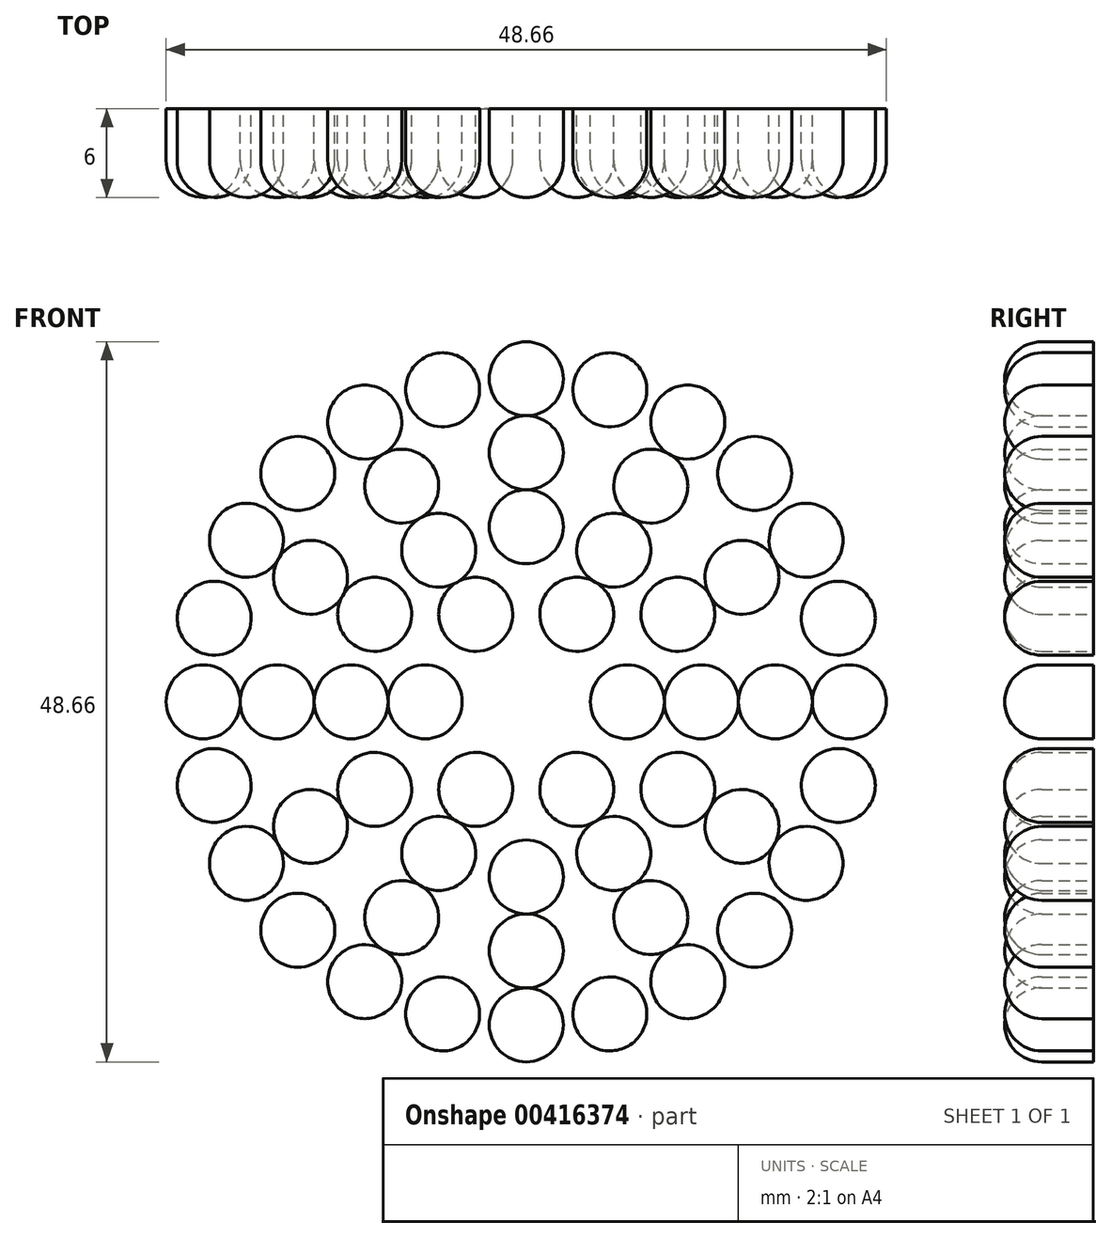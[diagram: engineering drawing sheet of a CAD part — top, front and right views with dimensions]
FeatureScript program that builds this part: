
annotation { "Feature Type Name" : "Feature", "Feature Type Description" : "" }
export const myFeature = defineFeature(function(context is Context, id is Id, definition is map)
    precondition{}
    {
        {
            var Q0;
            Q0=qCreatedBy(makeId("Front.planeOp"),FACE);
            var sketch = newSketch(context, id + "F0", { "sketchPlane" : qUnion([Q0])});
            skCircle(sketch, "E0.cCircle", {"center": v(0, 0) * mm, "radius": 9.33 * mm, "construction": true});
            skLineSegment(sketch, "E0.0", {"start": v(9.33, 2.5) * mm, "end": v(9.33, -2.5) * mm});
            skLineSegment(sketch, "E0.1", {"start": v(9.33, -2.5) * mm, "end": v(6.83, -6.83) * mm});
            skLineSegment(sketch, "E0.2", {"start": v(6.83, -6.83) * mm, "end": v(2.5, -9.33) * mm});
            skLineSegment(sketch, "E0.3", {"start": v(2.5, -9.33) * mm, "end": v(-2.5, -9.33) * mm});
            skLineSegment(sketch, "E0.4", {"start": v(-2.5, -9.33) * mm, "end": v(-6.83, -6.83) * mm});
            skLineSegment(sketch, "E0.5", {"start": v(-6.83, -6.83) * mm, "end": v(-9.33, -2.5) * mm});
            skLineSegment(sketch, "E0.6", {"start": v(-9.33, -2.5) * mm, "end": v(-9.33, 2.5) * mm});
            skLineSegment(sketch, "E0.7", {"start": v(-9.33, 2.5) * mm, "end": v(-6.83, 6.83) * mm});
            skLineSegment(sketch, "E0.8", {"start": v(-6.83, 6.83) * mm, "end": v(-2.5, 9.33) * mm});
            skLineSegment(sketch, "E0.9", {"start": v(-2.5, 9.33) * mm, "end": v(2.5, 9.33) * mm});
            skLineSegment(sketch, "E0.10", {"start": v(2.5, 9.33) * mm, "end": v(6.83, 6.83) * mm});
            skLineSegment(sketch, "E0.11", {"start": v(6.83, 6.83) * mm, "end": v(9.33, 2.5) * mm});
            skPoint(sketch, "E0.0.midPoint", {"position": v(9.33, 0) * mm});
            skLineSegment(sketch, "E1", {"start": v(-9.33, 2.5) * mm, "end": v(-4.33, 2.5) * mm});
            skLineSegment(sketch, "E2", {"start": v(-4.33, 2.5) * mm, "end": v(-6.83, 6.83) * mm});
            skLineSegment(sketch, "E3", {"start": v(-2.5, 9.33) * mm, "end": v(0, 5) * mm});
            skLineSegment(sketch, "E4", {"start": v(0, 5) * mm, "end": v(2.5, 9.33) * mm});
            skLineSegment(sketch, "E5", {"start": v(9.33, 2.5) * mm, "end": v(4.33, 2.5) * mm});
            skLineSegment(sketch, "E6", {"start": v(4.33, 2.5) * mm, "end": v(6.83, 6.83) * mm});
            skLineSegment(sketch, "E7", {"start": v(9.33, -2.5) * mm, "end": v(4.33, -2.5) * mm});
            skLineSegment(sketch, "E8", {"start": v(4.33, -2.5) * mm, "end": v(6.83, -6.83) * mm});
            skLineSegment(sketch, "E9", {"start": v(-9.33, -2.5) * mm, "end": v(-4.33, -2.5) * mm});
            skLineSegment(sketch, "E10", {"start": v(-4.33, -2.5) * mm, "end": v(-6.83, -6.83) * mm});
            skLineSegment(sketch, "E11", {"start": v(-2.5, -9.33) * mm, "end": v(0, -5) * mm});
            skLineSegment(sketch, "E12", {"start": v(0, -5) * mm, "end": v(2.5, -9.33) * mm});
            skLineSegment(sketch, "E13", {"start": v(0, 5) * mm, "end": v(4.33, 2.5) * mm});
            skLineSegment(sketch, "E14", {"start": v(4.33, 2.5) * mm, "end": v(4.33, -2.5) * mm});
            skLineSegment(sketch, "E15", {"start": v(4.33, -2.5) * mm, "end": v(0, -5) * mm});
            skLineSegment(sketch, "E16", {"start": v(0, -5) * mm, "end": v(-4.33, -2.5) * mm});
            skLineSegment(sketch, "E17", {"start": v(-4.33, -2.5) * mm, "end": v(-4.33, 2.5) * mm});
            skLineSegment(sketch, "E18", {"start": v(-4.33, 2.5) * mm, "end": v(0, 5) * mm});
            skLineSegment(sketch, "E19", {"start": v(-2.5, 9.33) * mm, "end": v(-2.5, 14.33) * mm});
            skLineSegment(sketch, "E20", {"start": v(-2.5, 14.33) * mm, "end": v(2.5, 14.33) * mm});
            skLineSegment(sketch, "E21", {"start": v(2.5, 14.33) * mm, "end": v(2.5, 9.33) * mm});
            skLineSegment(sketch, "E22", {"start": v(2.5, 9.33) * mm, "end": v(5, 13.66) * mm});
            skLineSegment(sketch, "E23", {"start": v(5, 13.66) * mm, "end": v(9.33, 11.16) * mm});
            skLineSegment(sketch, "E24", {"start": v(9.33, 11.16) * mm, "end": v(6.83, 6.83) * mm});
            skLineSegment(sketch, "E25", {"start": v(6.83, 6.83) * mm, "end": v(11.16, 9.33) * mm});
            skLineSegment(sketch, "E26", {"start": v(11.16, 9.33) * mm, "end": v(13.66, 5) * mm});
            skLineSegment(sketch, "E27", {"start": v(13.66, 5) * mm, "end": v(9.33, 2.5) * mm});
            skLineSegment(sketch, "E28", {"start": v(9.33, 2.5) * mm, "end": v(14.33, 2.5) * mm});
            skLineSegment(sketch, "E29", {"start": v(14.33, 2.5) * mm, "end": v(14.33, -2.5) * mm});
            skLineSegment(sketch, "E30", {"start": v(14.33, -2.5) * mm, "end": v(9.33, -2.5) * mm});
            skLineSegment(sketch, "E31", {"start": v(9.33, -2.5) * mm, "end": v(13.66, -5) * mm});
            skLineSegment(sketch, "E32", {"start": v(13.66, -5) * mm, "end": v(11.16, -9.33) * mm});
            skLineSegment(sketch, "E33", {"start": v(11.16, -9.33) * mm, "end": v(6.83, -6.83) * mm});
            skLineSegment(sketch, "E34", {"start": v(6.83, -6.83) * mm, "end": v(9.33, -11.16) * mm});
            skLineSegment(sketch, "E35", {"start": v(9.33, -11.16) * mm, "end": v(5, -13.66) * mm});
            skLineSegment(sketch, "E36", {"start": v(5, -13.66) * mm, "end": v(2.5, -9.33) * mm});
            skLineSegment(sketch, "E37", {"start": v(2.5, -9.33) * mm, "end": v(2.5, -14.33) * mm});
            skLineSegment(sketch, "E38", {"start": v(2.5, -14.33) * mm, "end": v(-2.5, -14.33) * mm});
            skLineSegment(sketch, "E39", {"start": v(-2.5, -14.33) * mm, "end": v(-2.5, -9.33) * mm});
            skLineSegment(sketch, "E40", {"start": v(-2.5, -9.33) * mm, "end": v(-5, -13.66) * mm});
            skLineSegment(sketch, "E41", {"start": v(-5, -13.66) * mm, "end": v(-9.33, -11.16) * mm});
            skLineSegment(sketch, "E42", {"start": v(-9.33, -11.16) * mm, "end": v(-6.83, -6.83) * mm});
            skLineSegment(sketch, "E43", {"start": v(-6.83, -6.83) * mm, "end": v(-11.16, -9.33) * mm});
            skLineSegment(sketch, "E44", {"start": v(-11.16, -9.33) * mm, "end": v(-13.66, -5) * mm});
            skLineSegment(sketch, "E45", {"start": v(-13.66, -5) * mm, "end": v(-9.33, -2.5) * mm});
            skLineSegment(sketch, "E46", {"start": v(-9.33, -2.5) * mm, "end": v(-14.33, -2.5) * mm});
            skLineSegment(sketch, "E47", {"start": v(-14.33, -2.5) * mm, "end": v(-14.33, 2.5) * mm});
            skLineSegment(sketch, "E48", {"start": v(-14.33, 2.5) * mm, "end": v(-9.33, 2.5) * mm});
            skLineSegment(sketch, "E49", {"start": v(-9.33, 2.5) * mm, "end": v(-13.66, 5) * mm});
            skLineSegment(sketch, "E50", {"start": v(-13.66, 5) * mm, "end": v(-11.16, 9.33) * mm});
            skLineSegment(sketch, "E51", {"start": v(-11.16, 9.33) * mm, "end": v(-6.83, 6.83) * mm});
            skLineSegment(sketch, "E52", {"start": v(-6.83, 6.83) * mm, "end": v(-9.33, 11.16) * mm});
            skLineSegment(sketch, "E53", {"start": v(-9.33, 11.16) * mm, "end": v(-5, 13.66) * mm});
            skLineSegment(sketch, "E54", {"start": v(-5, 13.66) * mm, "end": v(-2.5, 9.33) * mm});
            skLineSegment(sketch, "E55", {"start": v(14.33, 2.5) * mm, "end": v(19.33, 2.5) * mm});
            skLineSegment(sketch, "E56", {"start": v(19.33, 2.5) * mm, "end": v(24.33, 2.5) * mm});
            skLineSegment(sketch, "E57", {"start": v(24.33, 2.5) * mm, "end": v(24.33, -2.5) * mm});
            skLineSegment(sketch, "E58", {"start": v(19.33, 2.5) * mm, "end": v(19.33, -2.5) * mm});
            skCircle(sketch, "E59", {"center": v(0, 0) * mm, "radius": 4.33 * mm});
            skLineSegment(sketch, "E60", {"start": v(6.83, -2.5) * mm, "end": v(6.83, 0) * mm});
            skLineSegment(sketch, "E61", {"start": v(11.83, -2.5) * mm, "end": v(11.83, 0) * mm});
            skLineSegment(sketch, "E62", {"start": v(14.33, -2.5) * mm, "end": v(19.33, -2.5) * mm});
            skLineSegment(sketch, "E63", {"start": v(24.33, -2.5) * mm, "end": v(19.33, -2.5) * mm});
            skLineSegment(sketch, "E64", {"start": v(16.83, -2.5) * mm, "end": v(16.83, 0) * mm});
            skLineSegment(sketch, "E65", {"start": v(21.83, -2.5) * mm, "end": v(21.83, 0) * mm});
            skCircle(sketch, "E66", {"center": v(6.83, 0) * mm, "radius": 2.5 * mm});
            skCircle(sketch, "E67", {"center": v(11.83, 0) * mm, "radius": 2.5 * mm});
            skCircle(sketch, "E68", {"center": v(16.83, 0) * mm, "radius": 2.5 * mm});
            skCircle(sketch, "E69", {"center": v(21.83, 0) * mm, "radius": 2.5 * mm});
            skSolve(sketch);
        }
        {
            var Q0;
            Q0=qCreatedBy(makeId("Right.planeOp"),FACE);
            var sketch = newSketch(context, id + "F1", { "sketchPlane" : qUnion([Q0])});
            skLineSegment(sketch, "E70", {"start": v(30.42, 0) * mm, "end": v(-36.01, 0) * mm});
            skSolve(sketch);
        }
        {
            var Q0;
            {var subQ0=sQuery(id+"F0.wireOp",EDGE,"E66");var subQ1=makeQuery(id+"F0.imprint","INTERSECT",VERTEX,{"derivedFrom":[sQuery(id+"F0.wireOp",EDGE,"E5"),subQ0]});Q0=makeQuery(id+"F0.imprint","IMPRINT",FACE,{"disambiguationData":[TD([[makeQuery(id+"F0.imprint","IMPRINT",EDGE,{"disambiguationData":[TD([[subQ1,-1.0]])],"derivedFrom":subQ0}),1.0]])]});}
            var Q1;
            {var subQ0=sQuery(id+"F0.wireOp",EDGE,"E67");var subQ1=makeQuery(id+"F0.imprint","INTERSECT",VERTEX,{"derivedFrom":[sQuery(id+"F0.wireOp",EDGE,"E28"),subQ0]});Q1=makeQuery(id+"F0.imprint","IMPRINT",FACE,{"disambiguationData":[TD([[makeQuery(id+"F0.imprint","IMPRINT",EDGE,{"disambiguationData":[TD([[subQ1,1.0]])],"derivedFrom":subQ0}),1.0]])]});}
            var Q2;
            {var subQ0=sQuery(id+"F0.wireOp",EDGE,"E68");var subQ1=makeQuery(id+"F0.imprint","INTERSECT",VERTEX,{"derivedFrom":[sQuery(id+"F0.wireOp",EDGE,"E55"),subQ0]});Q2=makeQuery(id+"F0.imprint","IMPRINT",FACE,{"disambiguationData":[TD([[makeQuery(id+"F0.imprint","IMPRINT",EDGE,{"disambiguationData":[TD([[subQ1,1.0]])],"derivedFrom":subQ0}),1.0]])]});}
            var Q3;
            {var subQ0=sQuery(id+"F0.wireOp",EDGE,"E69");var subQ1=makeQuery(id+"F0.imprint","INTERSECT",VERTEX,{"derivedFrom":[sQuery(id+"F0.wireOp",EDGE,"E56"),subQ0]});Q3=makeQuery(id+"F0.imprint","IMPRINT",FACE,{"disambiguationData":[TD([[makeQuery(id+"F0.imprint","IMPRINT",EDGE,{"disambiguationData":[TD([[subQ1,1.0]])],"derivedFrom":subQ0}),1.0]])]});}
            extrude(context, id + "F2", {"entities" : qUnion([Q0, Q1, Q2, Q3]), "depth" : 6 * mm});
        }
        {
            var Q0;
            Q0=makeQuery(id+"F2.opExtrude","CAP_EDGE",EDGE,{"disambiguationData":[OSD([sQuery(id+"F0.wireOp",EDGE,"E66")])],"isStart":false});
            var Q1;
            Q1=makeQuery(id+"F2.opExtrude","CAP_EDGE",EDGE,{"disambiguationData":[OSD([sQuery(id+"F0.wireOp",EDGE,"E67")])],"isStart":false});
            var Q2;
            Q2=makeQuery(id+"F2.opExtrude","CAP_EDGE",EDGE,{"disambiguationData":[OSD([sQuery(id+"F0.wireOp",EDGE,"E68")])],"isStart":false});
            var Q3;
            Q3=makeQuery(id+"F2.opExtrude","CAP_EDGE",EDGE,{"disambiguationData":[OSD([sQuery(id+"F0.wireOp",EDGE,"E69")])],"isStart":false});
            fillet(context, id + "F3", {"entities" : qUnion([Q0, Q1, Q2, Q3]), "radius" : 2.5 * mm, "tangentPropagation" : true, "allowEdgeOverflow" : false});
        }
        {
            var Q0;
            Q0=makeQuery(id+"F2.opExtrude","SWEPT_BODY",BODY,{"disambiguationData":[OSD([sQuery(id+"F0.wireOp",EDGE,"E66")])]});
            var Q1;
            Q1=sQuery(id+"F1.wireOp",EDGE,"E70");
            circularPattern(context, id + "F4", {"entities" : qUnion([Q0]), "axis" : qUnion([Q1]), "angle" : 360 * degree, "instanceCount" : 6, "equalSpace" : true});
        }
        {
            var Q0;
            Q0=makeQuery(id+"F2.opExtrude","SWEPT_BODY",BODY,{"disambiguationData":[OSD([sQuery(id+"F0.wireOp",EDGE,"E67")])]});
            var Q1;
            Q1=makeQuery(id+"F2.opExtrude","SWEPT_BODY",BODY,{"disambiguationData":[OSD([sQuery(id+"F0.wireOp",EDGE,"E68")])]});
            var Q2;
            Q2=sQuery(id+"F1.wireOp",EDGE,"E70");
            circularPattern(context, id + "F5", {"entities" : qUnion([Q0, Q1]), "axis" : qUnion([Q2]), "angle" : 360 * degree, "instanceCount" : 12, "equalSpace" : true});
        }
        {
            var Q0;
            Q0=makeQuery(id+"F2.opExtrude","SWEPT_BODY",BODY,{"disambiguationData":[OSD([sQuery(id+"F0.wireOp",EDGE,"E69")])]});
            var Q1;
            Q1=sQuery(id+"F1.wireOp",EDGE,"E70");
            circularPattern(context, id + "F6", {"entities" : qUnion([Q0]), "axis" : qUnion([Q1]), "angle" : 360 * degree, "instanceCount" : 24, "equalSpace" : true});
        }
        {
            var Q0;
            Q0=sQuery(id+"F0.wireOp",EDGE,"E59");
            extrude(context, id + "F7", {"bodyType" : ToolBodyType.SURFACE, "surfaceEntities" : qUnion([Q0]), "oppositeDirection" : true, "depth" : 5 * mm, "hasSecondDirection" : true, "secondDirectionOppositeDirection" : false, "secondDirectionDepth" : 3 * mm});
        }
    });
